FCSTD DOCUMENT  (FreeCAD 0.17R13522 (Git))
Label: SPECTRO_PLONGEUR_7
License: All rights reserved
LicenseURL: http://en.wikipedia.org/wiki/All_rights_reserved
objects: Sketcher::SketchObject×3, PartDesign::Body×1
note: 4 computed .brp shape members not serialized (recipe doc carries the construction recipe); baked Part::Feature solids carry a one-line shape summary decoded from their .brp

FEATURE [Sketcher::SketchObject] Sketch001  label="flat_7.1"
  MapMode = 5
  Support = -> [XY_Plane]
  sketch-geometry (44):
    g0: LineSegment StartX=0 StartY=0 StartZ=0 EndX=-12 EndY=0 EndZ=0
    g1: LineSegment StartX=-12 StartY=0 StartZ=0 EndX=-12 EndY=-137 EndZ=0
    g2: LineSegment StartX=-14 StartY=-139 StartZ=0 EndX=-71.5 EndY=-139 EndZ=0
    g3: LineSegment StartX=-73.5 StartY=-141 StartZ=0 EndX=-73.5 EndY=-169 EndZ=0
    g4: LineSegment StartX=-71.5 StartY=-171 StartZ=0 EndX=-65 EndY=-171 EndZ=0
    g5: LineSegment StartX=-63 StartY=-169 StartZ=0 EndX=-63 EndY=-152 EndZ=0
    g6: LineSegment StartX=-61 StartY=-150 StartZ=0 EndX=-41 EndY=-150 EndZ=0
    g7: LineSegment StartX=-39 StartY=-152 StartZ=0 EndX=-39 EndY=-165 EndZ=0
    g8: LineSegment StartX=-39 StartY=-165 StartZ=0 EndX=-29 EndY=-168 EndZ=0
    g9: LineSegment StartX=-29 StartY=-168 StartZ=0 EndX=-29 EndY=-178 EndZ=0
    g10: LineSegment StartX=-27 StartY=-180 StartZ=0 EndX=-2 EndY=-180 EndZ=0
    g11: LineSegment StartX=0 StartY=-178 StartZ=0 EndX=0 EndY=0 EndZ=0
    g12: ArcOfCircle CenterX=-71.5 CenterY=-141 CenterZ=0 NormalX=0 NormalY=0 NormalZ=1 AngleXU=0 Radius=2 StartAngle=1.5708 EndAngle=3.14159
    g13: ArcOfCircle CenterX=-14 CenterY=-137 CenterZ=0 NormalX=0 NormalY=0 NormalZ=1 AngleXU=0 Radius=2 StartAngle=4.71239 EndAngle=6.28319
    g14: ArcOfCircle CenterX=-71.5 CenterY=-169 CenterZ=0 NormalX=0 NormalY=0 NormalZ=1 AngleXU=0 Radius=2 StartAngle=3.14159 EndAngle=4.71239
    g15: ArcOfCircle CenterX=-65 CenterY=-169 CenterZ=0 NormalX=0 NormalY=0 NormalZ=1 AngleXU=0 Radius=2 StartAngle=4.71239 EndAngle=6.28319
    g16: ArcOfCircle CenterX=-41 CenterY=-152 CenterZ=0 NormalX=0 NormalY=0 NormalZ=1 AngleXU=0 Radius=2 StartAngle=0 EndAngle=1.5708
    g17: ArcOfCircle CenterX=-61 CenterY=-152 CenterZ=0 NormalX=0 NormalY=0 NormalZ=1 AngleXU=0 Radius=2 StartAngle=1.5708 EndAngle=3.14159
    g18: ArcOfCircle CenterX=-27 CenterY=-178 CenterZ=0 NormalX=0 NormalY=0 NormalZ=1 AngleXU=0 Radius=2 StartAngle=3.14159 EndAngle=4.71239
    g19: ArcOfCircle CenterX=-2 CenterY=-178 CenterZ=0 NormalX=0 NormalY=0 NormalZ=1 AngleXU=0 Radius=2 StartAngle=4.71239 EndAngle=6.28319
    g20: LineSegment StartX=-66 StartY=-167 StartZ=0 EndX=-70 EndY=-167 EndZ=0
    g21: LineSegment StartX=-70 StartY=-167 StartZ=0 EndX=-70 EndY=-144.5 EndZ=0
    g22: LineSegment StartX=-68 StartY=-142.5 StartZ=0 EndX=-10.5 EndY=-142.5 EndZ=0
    g23: LineSegment StartX=-8.5 StartY=-140.5 StartZ=0 EndX=-8.5 EndY=0 EndZ=0
    g24: LineSegment StartX=-8.5 StartY=0 StartZ=0 EndX=-3.5 EndY=0 EndZ=0
    g25: LineSegment StartX=-3.5 StartY=0 StartZ=0 EndX=-3.5 EndY=-174 EndZ=0
    g26: LineSegment StartX=-5.5 StartY=-176 StartZ=0 EndX=-29 EndY=-176 EndZ=0
    g27: LineSegment StartX=-29 StartY=-176 StartZ=0 EndX=-29 EndY=-172 EndZ=0
    g28: LineSegment StartX=-29 StartY=-172 StartZ=0 EndX=-10.5 EndY=-172 EndZ=0
    g29: LineSegment StartX=-8.5 StartY=-170 StartZ=0 EndX=-8.5 EndY=-161 EndZ=0
    g30: LineSegment StartX=-8.5 StartY=-161 StartZ=0 EndX=-39.1 EndY=-161 EndZ=0
    g31: LineSegment StartX=-39.1 StartY=-161 StartZ=0 EndX=-39.1 EndY=-157 EndZ=0
    g32: LineSegment StartX=-39.1 StartY=-157 StartZ=0 EndX=-10.5 EndY=-157 EndZ=0
    g33: LineSegment StartX=-8.5 StartY=-155 StartZ=0 EndX=-8.5 EndY=-146.5 EndZ=0
    g34: LineSegment StartX=-8.5 StartY=-146.5 StartZ=0 EndX=-65 EndY=-146.5 EndZ=0
    g35: LineSegment StartX=-67 StartY=-148.5 StartZ=0 EndX=-67 EndY=-161 EndZ=0
    g36: LineSegment StartX=-67 StartY=-161 StartZ=0 EndX=-66 EndY=-161 EndZ=0
    g37: LineSegment StartX=-66 StartY=-161 StartZ=0 EndX=-66 EndY=-167 EndZ=0
    g38: ArcOfCircle CenterX=-68 CenterY=-144.5 CenterZ=0 NormalX=0 NormalY=0 NormalZ=1 AngleXU=0 Radius=2 StartAngle=1.5708 EndAngle=3.14159
    g39: ArcOfCircle CenterX=-65 CenterY=-148.5 CenterZ=0 NormalX=0 NormalY=0 NormalZ=1 AngleXU=0 Radius=2 StartAngle=1.5708 EndAngle=3.14159
    g40: ArcOfCircle CenterX=-10.5 CenterY=-155 CenterZ=0 NormalX=0 NormalY=0 NormalZ=1 AngleXU=0 Radius=2 StartAngle=4.71239 EndAngle=6.28319
    g41: ArcOfCircle CenterX=-10.5 CenterY=-170 CenterZ=0 NormalX=0 NormalY=0 NormalZ=1 AngleXU=0 Radius=2 StartAngle=4.71239 EndAngle=6.28319
    g42: ArcOfCircle CenterX=-5.5 CenterY=-174 CenterZ=0 NormalX=0 NormalY=0 NormalZ=1 AngleXU=0 Radius=2 StartAngle=4.71239 EndAngle=6.28319
    g43: ArcOfCircle CenterX=-10.5 CenterY=-140.5 CenterZ=0 NormalX=0 NormalY=0 NormalZ=1 AngleXU=0 Radius=2 StartAngle=4.71239 EndAngle=6.28319
  constraints (117):
    c: Coincident(g-1,g0)
    c: Coincident(g0,g1)
    c: Horizontal(g2)
    c: Vertical(g3)
    c: Horizontal(g4)
    c: Vertical(g5)
    c: Horizontal(g6)
    c: Coincident(g7,g8)
    c: Coincident(g8,g9)
    c: Vertical(g9)
    c: Horizontal(g10)
    c: Coincident(g11,g0)
    c: Vertical(g11)
    c: Tangent(g2,g12) = -1.5708
    c: Tangent(g3,g12) = -1.5708
    c: Tangent(g1,g13) = 1.5708
    c: Tangent(g2,g13) = 1.5708
    c: Tangent(g3,g14) = -1.5708
    c: Tangent(g4,g14) = -1.5708
    c: Tangent(g4,g15) = -1.5708
    c: Tangent(g5,g15) = -1.5708
    c: Tangent(g6,g16) = 1.5708
    c: Tangent(g7,g16) = 1.5708
    c: Tangent(g5,g17) = 1.5708
    c: Tangent(g6,g17) = 1.5708
    c: Tangent(g9,g18) = -1.5708
    c: Tangent(g10,g18) = -1.5708
    c: Tangent(g10,g19) = -1.5708
    c: Tangent(g11,g19) = -1.5708
    c: Radius(g13) = 2
    c: Equal(g13,g12)
    c: Equal(g13,g14)
    c: Equal(g13,g15)
    c: Equal(g13,g17)
    c: Equal(g13,g16)
    c: Equal(g13,g18)
    c: Equal(g13,g19)
    c: Distance(g3) = 28
    c: Distance(g4) = 6.5
    c: Distance(g5) = 17
    c: Distance(g6) = 20
    c: Distance(g7) = 13
    c: DistanceY(g8,g8) = 3
    c: DistanceX(g8,g8) = 10
    c: Distance(g9) = 10
    c: Distance(g10) = 25
    c: Distance(g11) = 178
    c: Distance(g1) = 137
    c: Distance(g0) = 12
    c: Vertical(g1)
    c: Horizontal(g0)
    c: Horizontal(g20)
    c: Coincident(g20,g21)
    c: Horizontal(g22)
    c: Vertical(g23)
    c: Coincident(g23,g24)
    c: Coincident(g24,g25)
    c: Vertical(g25)
    c: Coincident(g26,g27)
    c: Coincident(g27,g28)
    c: Horizontal(g28)
    c: Vertical(g29)
    c: Coincident(g29,g30)
    c: Horizontal(g30)
    c: Coincident(g30,g31)
    c: Coincident(g31,g32)
    c: Vertical(g33)
    c: Coincident(g33,g34)
    c: Coincident(g35,g36)
    c: Horizontal(g36)
    c: Coincident(g36,g37)
    c: Coincident(g37,g20)
    c: Vertical(g37)
    c: Tangent(g21,g38) = 1.5708
    c: Tangent(g22,g38) = 1.5708
    c: Tangent(g34,g39) = -1.5708
    c: Tangent(g35,g39) = -1.5708
    c: Tangent(g32,g40) = -1.5708
    c: Tangent(g33,g40) = -1.5708
    c: Tangent(g28,g41) = -1.5708
    c: Tangent(g29,g41) = -1.5708
    c: Tangent(g25,g42) = 1.5708
    c: Tangent(g26,g42) = 1.5708
    c: Tangent(g22,g43) = -1.5708
    c: Tangent(g23,g43) = -1.5708
    c: Distance(g21) = 22.5
    c: Distance(g35) = 12.5
    c: Distance(g22) = 57.5
    c: Distance(g34) = 56.5
    c: Distance(g36) = 1
    c: Distance(g37) = 6
    c: Distance(g20) = 4
    c: Distance(g23) = 140.5
    c: Distance(g25) = 174
    c: Distance(g26) = 23.5
    c: Distance(g27) = 4
    c: Distance(g28) = 18.5
    c: Distance(g29) = 9
    c: Distance(g30) = 30.6
    c: Distance(g31) = 4
    c: Distance(g33) = 8.5
    c: Distance(g24) = 5
    c: Vertical(g21)
    c: Vertical(g35)
    c: Horizontal(g34)
    c: Radius(g38) = 2
    c: Equal(g38,g39)
    c: Equal(g38,g40)
    c: Equal(g38,g42)
    c: Equal(g38,g41)
    c: Equal(g38,g43)
    c: Horizontal(g32)
    c: Horizontal(g24)
    c: Vertical(g31)
    c: DistanceY(g-1,g24) = 0
    c: DistanceX(g24,g-1) = 3.5
    c: Distance(g32) = 28.6
FEATURE [Sketcher::SketchObject] Sketch  label="flat_7.2"
  MapMode = 5
  Support = -> [XY_Plane]
  sketch-geometry (50):
    g0: LineSegment StartX=40 StartY=0 StartZ=0 EndX=40 EndY=-178 EndZ=0
    g1: LineSegment StartX=42 StartY=-180 StartZ=0 EndX=67 EndY=-180 EndZ=0
    g2: LineSegment StartX=69 StartY=-178 StartZ=0 EndX=69 EndY=-168 EndZ=0
    g3: LineSegment StartX=69 StartY=-168 StartZ=0 EndX=79 EndY=-165 EndZ=0
    g4: LineSegment StartX=79 StartY=-165 StartZ=0 EndX=79 EndY=-152 EndZ=0
    g5: LineSegment StartX=81 StartY=-150 StartZ=0 EndX=101 EndY=-150 EndZ=0
    g6: LineSegment StartX=103 StartY=-152 StartZ=0 EndX=103 EndY=-169 EndZ=0
    g7: LineSegment StartX=105 StartY=-171 StartZ=0 EndX=111.5 EndY=-171 EndZ=0
    g8: LineSegment StartX=113.5 StartY=-169 StartZ=0 EndX=113.5 EndY=-141 EndZ=0
    g9: LineSegment StartX=111.5 StartY=-139 StartZ=0 EndX=54 EndY=-139 EndZ=0
    g10: LineSegment StartX=52 StartY=-137 StartZ=0 EndX=52 EndY=0 EndZ=0
    g11: LineSegment StartX=52 StartY=0 StartZ=0 EndX=40 EndY=0 EndZ=0
    g12: ArcOfCircle CenterX=42 CenterY=-178 CenterZ=0 NormalX=0 NormalY=0 NormalZ=1 AngleXU=0 Radius=2 StartAngle=3.14159 EndAngle=4.71239
    g13: ArcOfCircle CenterX=67 CenterY=-178 CenterZ=0 NormalX=0 NormalY=0 NormalZ=1 AngleXU=0 Radius=2 StartAngle=4.71239 EndAngle=6.28319
    g14: ArcOfCircle CenterX=81 CenterY=-152 CenterZ=0 NormalX=0 NormalY=0 NormalZ=1 AngleXU=0 Radius=2 StartAngle=1.5708 EndAngle=3.14159
    g15: ArcOfCircle CenterX=101 CenterY=-152 CenterZ=0 NormalX=0 NormalY=0 NormalZ=1 AngleXU=0 Radius=2 StartAngle=0 EndAngle=1.5708
    g16: ArcOfCircle CenterX=105 CenterY=-169 CenterZ=0 NormalX=0 NormalY=0 NormalZ=1 AngleXU=0 Radius=2 StartAngle=3.14159 EndAngle=4.71239
    g17: ArcOfCircle CenterX=111.5 CenterY=-169 CenterZ=0 NormalX=0 NormalY=0 NormalZ=1 AngleXU=0 Radius=2 StartAngle=4.71239 EndAngle=6.28319
    g18: ArcOfCircle CenterX=111.5 CenterY=-141 CenterZ=0 NormalX=0 NormalY=0 NormalZ=1 AngleXU=0 Radius=2 StartAngle=0 EndAngle=1.5708
    g19: ArcOfCircle CenterX=54 CenterY=-137 CenterZ=0 NormalX=0 NormalY=0 NormalZ=1 AngleXU=0 Radius=2 StartAngle=3.14159 EndAngle=4.71239
    g20: LineSegment StartX=43.5 StartY=0 StartZ=0 EndX=43.5 EndY=-174 EndZ=0
    g21: LineSegment StartX=45.5 StartY=-176 StartZ=0 EndX=69 EndY=-176 EndZ=0
    g22: LineSegment StartX=69 StartY=-176 StartZ=0 EndX=69 EndY=-172 EndZ=0
    g23: LineSegment StartX=69 StartY=-172 StartZ=0 EndX=50.5 EndY=-172 EndZ=0
    g24: LineSegment StartX=48.5 StartY=-170 StartZ=0 EndX=48.5 EndY=-161 EndZ=0
    g25: LineSegment StartX=48.5 StartY=-161 StartZ=0 EndX=79 EndY=-161 EndZ=0
    g26: LineSegment StartX=79 StartY=-161 StartZ=0 EndX=79 EndY=-157 EndZ=0
    g27: LineSegment StartX=79 StartY=-157 StartZ=0 EndX=50.5 EndY=-157 EndZ=0
    g28: LineSegment StartX=48.5 StartY=-155 StartZ=0 EndX=48.5 EndY=-146.5 EndZ=0
    g29: LineSegment StartX=48.5 StartY=-146.5 StartZ=0 EndX=105 EndY=-146.5 EndZ=0
    g30: LineSegment StartX=107 StartY=-148.5 StartZ=0 EndX=107 EndY=-161 EndZ=0
    g31: LineSegment StartX=107 StartY=-161 StartZ=0 EndX=106 EndY=-161 EndZ=0
    g32: LineSegment StartX=106 StartY=-161 StartZ=0 EndX=106 EndY=-167 EndZ=0
    g33: LineSegment StartX=106 StartY=-167 StartZ=0 EndX=110 EndY=-167 EndZ=0
    g34: LineSegment StartX=110 StartY=-167 StartZ=0 EndX=110 EndY=-144.5 EndZ=0
    g35: LineSegment StartX=108 StartY=-142.5 StartZ=0 EndX=50.5 EndY=-142.5 EndZ=0
    g36: LineSegment StartX=48.5 StartY=-140.5 StartZ=0 EndX=48.5 EndY=0 EndZ=0
    g37: LineSegment StartX=48.5 StartY=0 StartZ=0 EndX=43.5 EndY=0 EndZ=0
    g38: ArcOfCircle CenterX=50.5 CenterY=-170 CenterZ=0 NormalX=0 NormalY=0 NormalZ=1 AngleXU=0 Radius=2 StartAngle=3.14159 EndAngle=4.71239
    g39: ArcOfCircle CenterX=50.5 CenterY=-155 CenterZ=0 NormalX=0 NormalY=0 NormalZ=1 AngleXU=0 Radius=2 StartAngle=3.14159 EndAngle=4.71239
    g40: ArcOfCircle CenterX=45.5 CenterY=-174 CenterZ=0 NormalX=0 NormalY=0 NormalZ=1 AngleXU=0 Radius=2 StartAngle=3.14159 EndAngle=4.71239
    g41: ArcOfCircle CenterX=50.5 CenterY=-140.5 CenterZ=0 NormalX=0 NormalY=0 NormalZ=1 AngleXU=0 Radius=2 StartAngle=3.14159 EndAngle=4.71239
    g42: ArcOfCircle CenterX=105 CenterY=-148.5 CenterZ=0 NormalX=0 NormalY=0 NormalZ=1 AngleXU=0 Radius=2 StartAngle=0 EndAngle=1.5708
    g43: ArcOfCircle CenterX=108 CenterY=-144.5 CenterZ=0 NormalX=0 NormalY=0 NormalZ=1 AngleXU=0 Radius=2 StartAngle=0 EndAngle=1.5708
    g44: LineSegment StartX=106.05 StartY=-161 StartZ=0 EndX=106.05 EndY=-167 EndZ=0
    g45: LineSegment StartX=106.05 StartY=-167 StartZ=0 EndX=110.05 EndY=-167 EndZ=0
    g46: LineSegment StartX=110.05 StartY=-167 StartZ=0 EndX=110.05 EndY=-147 EndZ=0
    g47: LineSegment StartX=110.05 StartY=-147 StartZ=0 EndX=107.05 EndY=-147 EndZ=0
    g48: LineSegment StartX=107.05 StartY=-147 StartZ=0 EndX=107.05 EndY=-161 EndZ=0
    g49: LineSegment StartX=107.05 StartY=-161 StartZ=0 EndX=106.05 EndY=-161 EndZ=0
  constraints (132):
    c: PointOnObject(g0,g-1)
    c: Vertical(g0)
    c: Horizontal(g1)
    c: Coincident(g2,g3)
    c: Coincident(g3,g4)
    c: Vertical(g4)
    c: Horizontal(g5)
    c: Horizontal(g7)
    c: Vertical(g8)
    c: Vertical(g10)
    c: Coincident(g10,g11)
    c: Coincident(g11,g0)
    c: Horizontal(g11)
    c: Tangent(g0,g12) = -1.5708
    c: Tangent(g1,g12) = -1.5708
    c: Tangent(g1,g13) = -1.5708
    c: Tangent(g2,g13) = -1.5708
    c: Tangent(g4,g14) = 1.5708
    c: Tangent(g5,g14) = 1.5708
    c: Tangent(g5,g15) = 1.5708
    c: Tangent(g6,g15) = 1.5708
    c: Tangent(g6,g16) = -1.5708
    c: Tangent(g7,g16) = -1.5708
    c: Tangent(g7,g17) = -1.5708
    c: Tangent(g8,g17) = -1.5708
    c: Tangent(g8,g18) = -1.5708
    c: Tangent(g9,g18) = -1.5708
    c: Tangent(g9,g19) = 1.5708
    c: Tangent(g10,g19) = 1.5708
    c: Distance(g11) = 12
    c: Radius(g19) = 2
    c: Equal(g19,g12)
    c: Equal(g19,g18)
    c: Equal(g19, g13-g17) x5
    c: Distance(g10) = 137
    c: Distance(g9) = 57.5
    c: Distance(g8) = 28
    c: Distance(g7) = 6.5
    c: Distance(g6) = 17
    c: Distance(g5) = 20
    c: Distance(g4) = 13
    c: DistanceY(g3,g3) = 3
    c: DistanceX(g3,g3) = 10
    c: Distance(g2) = 10
    c: Distance(g1) = 25
    c: Distance(g0) = 178
    c: Vertical(g2)
    c: Distance(g-1,g0) = 40
    c: Horizontal(g21)
    c: Coincident(g21,g22)
    c: Vertical(g22)
    c: Coincident(g22,g23)
    c: Horizontal(g23)
    c: Coincident(g24,g25)
    c: Horizontal(g25)
    c: Coincident(g25,g26)
    c: Vertical(g26)
    c: Coincident(g26,g27)
    c: Horizontal(g27)
    c: Coincident(g28,g29)
    c: Horizontal(g29)
    c: Vertical(g30)
    c: Coincident(g30,g31)
    c: Coincident(g31,g32)
    c: Coincident(g32,g33)
    c: Horizontal(g33)
    c: Coincident(g33,g34)
    c: Horizontal(g35)
    c: Coincident(g36,g37)
    c: Coincident(g37,g20)
    c: Tangent(g23,g38) = 1.5708
    c: Tangent(g24,g38) = 1.5708
    c: Tangent(g27,g39) = 1.5708
    c: Tangent(g28,g39) = 1.5708
    c: Tangent(g20,g40) = -1.5708
    c: Tangent(g21,g40) = -1.5708
    c: Tangent(g35,g41) = 1.5708
    c: Tangent(g36,g41) = 1.5708
    c: Tangent(g29,g42) = 1.5708
    c: Tangent(g30,g42) = 1.5708
    c: Tangent(g34,g43) = -1.5708
    c: Tangent(g35,g43) = -1.5708
    c: Radius(g40) = 2
    c: Equal(g40,g38)
    c: Equal(g40,g39)
    c: Equal(g40,g41)
    c: Equal(g40,g42)
    c: Equal(g40,g43)
    c: Distance(g37) = 5
    c: Distance(g36) = 140.5
    c: Distance(g20) = 174
    c: Distance(g35) = 57.5
    c: Distance(g34) = 22.5
    c: Distance(g32) = 6
    c: Distance(g31) = 1
    c: Distance(g30) = 12.5
    c: Distance(g29) = 56.5
    c: Distance(g28) = 8.5
    c: Distance(g26) = 4
    c: Distance(g24) = 9
    c: Distance(g22) = 4
    c: Distance(g21) = 23.5
    c: Horizontal(g31)
    c: Vertical(g32)
    c: Vertical(g34)
    c: Vertical(g28)
    c: Distance(g25) = 30.5
    c: Distance(g27) = 28.5
    c: Vertical(g24)
    c: Vertical(g36)
    c: Vertical(g20)
    c: DistanceY(g1,g21) = 4
    c: DistanceX(g0,g20) = 3.5
    c: Distance(g23) = 18.5
    c: Vertical(g44)
    c: Coincident(g44,g45)
    c: Horizontal(g45)
    c: Coincident(g45,g46)
    c: Vertical(g46)
    c: Coincident(g46,g47)
    c: Coincident(g47,g48)
    c: Vertical(g48)
    c: Coincident(g48,g49)
    c: Coincident(g49,g44)
    c: Horizontal(g49)
    c: Distance(g44) = 6
    c: Distance(g45) = 4
    c: Distance(g49) = 1
    c: Distance(g46) = 20
    c: Distance(g47) = 3
    c: DistanceX(g32,g44) = 0.05
    c: DistanceY(g32,g44) = 0
FEATURE [Sketcher::SketchObject] Sketch002  label="flat_7.3"
  MapMode = 5
  Support = -> [XY_Plane]
  sketch-geometry (20):
    g0: LineSegment StartX=212 StartY=0 StartZ=0 EndX=212 EndY=-178 EndZ=0
    g1: LineSegment StartX=210 StartY=-180 StartZ=0 EndX=185 EndY=-180 EndZ=0
    g2: LineSegment StartX=183 StartY=-178 StartZ=0 EndX=183 EndY=-168 EndZ=0
    g3: LineSegment StartX=183 StartY=-168 StartZ=0 EndX=173 EndY=-165 EndZ=0
    g4: LineSegment StartX=173 StartY=-165 StartZ=0 EndX=173 EndY=-152 EndZ=0
    g5: LineSegment StartX=171 StartY=-150 StartZ=0 EndX=151 EndY=-150 EndZ=0
    g6: LineSegment StartX=149 StartY=-152 StartZ=0 EndX=149 EndY=-169 EndZ=0
    g7: LineSegment StartX=147 StartY=-171 StartZ=0 EndX=140.5 EndY=-171 EndZ=0
    g8: LineSegment StartX=138.5 StartY=-169 StartZ=0 EndX=138.5 EndY=-141 EndZ=0
    g9: LineSegment StartX=140.5 StartY=-139 StartZ=0 EndX=198 EndY=-139 EndZ=0
    g10: LineSegment StartX=200 StartY=-137 StartZ=0 EndX=200 EndY=0 EndZ=0
    g11: LineSegment StartX=200 StartY=0 StartZ=0 EndX=212 EndY=0 EndZ=0
    g12: ArcOfCircle CenterX=198 CenterY=-137 CenterZ=0 NormalX=0 NormalY=0 NormalZ=1 AngleXU=0 Radius=2 StartAngle=4.71239 EndAngle=6.28319
    g13: ArcOfCircle CenterX=210 CenterY=-178 CenterZ=0 NormalX=0 NormalY=0 NormalZ=1 AngleXU=0 Radius=2 StartAngle=4.71239 EndAngle=6.28319
    g14: ArcOfCircle CenterX=185 CenterY=-178 CenterZ=0 NormalX=0 NormalY=0 NormalZ=1 AngleXU=0 Radius=2 StartAngle=3.14159 EndAngle=4.71239
    g15: ArcOfCircle CenterX=171 CenterY=-152 CenterZ=0 NormalX=0 NormalY=0 NormalZ=1 AngleXU=0 Radius=2 StartAngle=0 EndAngle=1.5708
    g16: ArcOfCircle CenterX=151 CenterY=-152 CenterZ=0 NormalX=0 NormalY=0 NormalZ=1 AngleXU=0 Radius=2 StartAngle=1.5708 EndAngle=3.14159
    g17: ArcOfCircle CenterX=147 CenterY=-169 CenterZ=0 NormalX=0 NormalY=0 NormalZ=1 AngleXU=0 Radius=2 StartAngle=4.71239 EndAngle=6.28319
    g18: ArcOfCircle CenterX=140.5 CenterY=-169 CenterZ=0 NormalX=0 NormalY=0 NormalZ=1 AngleXU=0 Radius=2 StartAngle=3.14159 EndAngle=4.71239
    g19: ArcOfCircle CenterX=140.5 CenterY=-141 CenterZ=0 NormalX=0 NormalY=0 NormalZ=1 AngleXU=0 Radius=2 StartAngle=1.5708 EndAngle=3.14159
  constraints (52):
    c: Vertical(g0)
    c: Horizontal(g1)
    c: Vertical(g2)
    c: Coincident(g2,g3)
    c: Coincident(g3,g4)
    c: Vertical(g4)
    c: Horizontal(g5)
    c: Horizontal(g9)
    c: Vertical(g10)
    c: Coincident(g10,g11)
    c: Coincident(g11,g0)
    c: Distance(g11) = 12
    c: Tangent(g9,g12) = -1.5708
    c: Tangent(g10,g12) = -1.5708
    c: Tangent(g0,g13) = 1.5708
    c: Tangent(g1,g13) = 1.5708
    c: Tangent(g1,g14) = 1.5708
    c: Tangent(g2,g14) = 1.5708
    c: Tangent(g4,g15) = -1.5708
    c: Tangent(g5,g15) = -1.5708
    c: Tangent(g5,g16) = -1.5708
    c: Tangent(g6,g16) = -1.5708
    c: Tangent(g6,g17) = 1.5708
    c: Tangent(g7,g17) = 1.5708
    c: Tangent(g7,g18) = 1.5708
    c: Tangent(g8,g18) = 1.5708
    c: Tangent(g8,g19) = 1.5708
    c: Tangent(g9,g19) = 1.5708
    c: Radius(g19) = 2
    c: Equal(g19,g18)
    c: Equal(g19,g17)
    c: Equal(g19,g15)
    c: Equal(g19,g16)
    c: Equal(g19,g14)
    c: Equal(g19,g13)
    c: Equal(g19,g12)
    c: Distance(g0) = 178
    c: Distance(g1) = 25
    c: Distance(g2) = 10
    c: DistanceY(g3,g3) = 3
    c: DistanceX(g3,g3) = 10
    c: Distance(g4) = 13
    c: Distance(g5) = 20
    c: Distance(g6) = 17
    c: Distance(g7) = 6.5
    c: Distance(g8) = 28
    c: Distance(g9) = 57.5
    c: Distance(g10) = 137
    c: Vertical(g8)
    c: Horizontal(g7)
    c: DistanceY(g-1,g10) = 0
    c: DistanceX(g-1,g10) = 200
FEATURE [PartDesign::Body] Body
  Group = -> [Sketch001,Sketch,Sketch002]
  Origin = -> Origin
